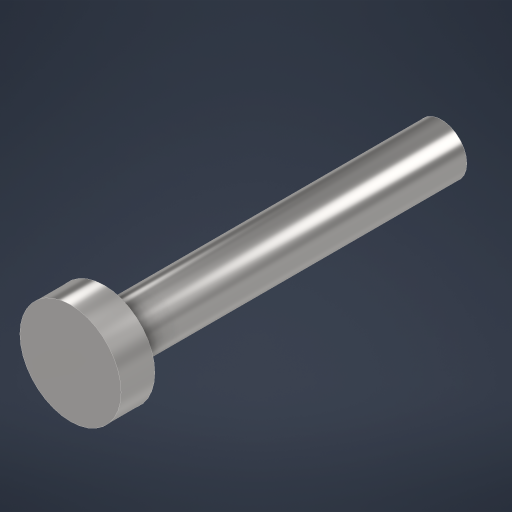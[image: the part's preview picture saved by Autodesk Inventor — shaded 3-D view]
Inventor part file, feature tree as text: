
AUTODESK INVENTOR PART (.ipt)
format: ipt  version: 2023.2 (Build 272271000, 271)  size: 240,640 bytes
history: native  units: mm
features: revolve x1, sketch x1
ambient origin geometry x8: Origin, YZ Plane, XZ Plane, XY Plane, X Axis, Y Axis, Z Axis, Center Point
bodies: Body1 (feature_tree)
feature tree (2):
  revolve  "Revolution1"  [1 undecoded]
  sketch  "Sketch1"  dims[d230=1.0mm d231=3.0mm d233=10.0mm d235=90.0deg d236=1.5mm d9=0.5mm d10=0.872665mm d11=0.5mm d12=0.872665mm d13=0.5mm d14=0.872665mm d27=0.5mm d28=0.872665mm d29=0.5mm d30=0.872665mm d88=0.5mm d89=0.872665mm d90=0.5mm d91=0.872665mm d116=0.5mm d117=0.872665mm d118=0.5mm d119=0.872665mm d154=0.5mm d155=0.872665mm d156=0.5mm d157=0.872665mm d181=0.5mm d182=0.872665mm d183=0.5mm d184=0.872665mm d221=0.5mm d222=0.872665mm d223=0.5mm d224=0.872665mm]
note: 1 required parameter value undecoded (feature->parameter linkage not recoverable at this tier; creation-order binding heuristic only, values carry confidence <= 0.55)
